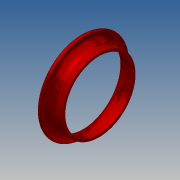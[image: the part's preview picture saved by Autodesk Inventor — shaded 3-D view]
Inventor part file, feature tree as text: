
AUTODESK INVENTOR PART (.ipt)
format: ipt  version: 2017.3 (Build 213257000, 257)  size: 180,736 bytes
history: native  units: in
note: dims shown in document units (in); Inventor stores cm internally (conversion verified against a paired STEP export)
features: other x3, extrude x2, sketch x1
ambient origin geometry x8: Origin, YZ Plane, XZ Plane, XY Plane, X Axis, Y Axis, Z Axis, Center Point
bodies: Solid1 (feature_tree)
feature tree (6):
  other  "A1-19027-500-02 HCWI nozzle horn.ipt"
  sketch  "Sketch2"  dims[d0=0.3937in d1=0.5in d2=0.5in d3=0.0in d4=0.0in d5=0.5in d6=2.125in d7=0.0in d8=0.0in]
  extrude  "Extrusion1"  Depth=0.3937in TaperAngle=0.0deg
  extrude  "Extrusion2"  Depth=0.3937in TaperAngle=0.0deg
  other  "Solid1::A1-19027-500-02 HCWI nozzle horn.ipt"
  other  "TaggingFeature1"
